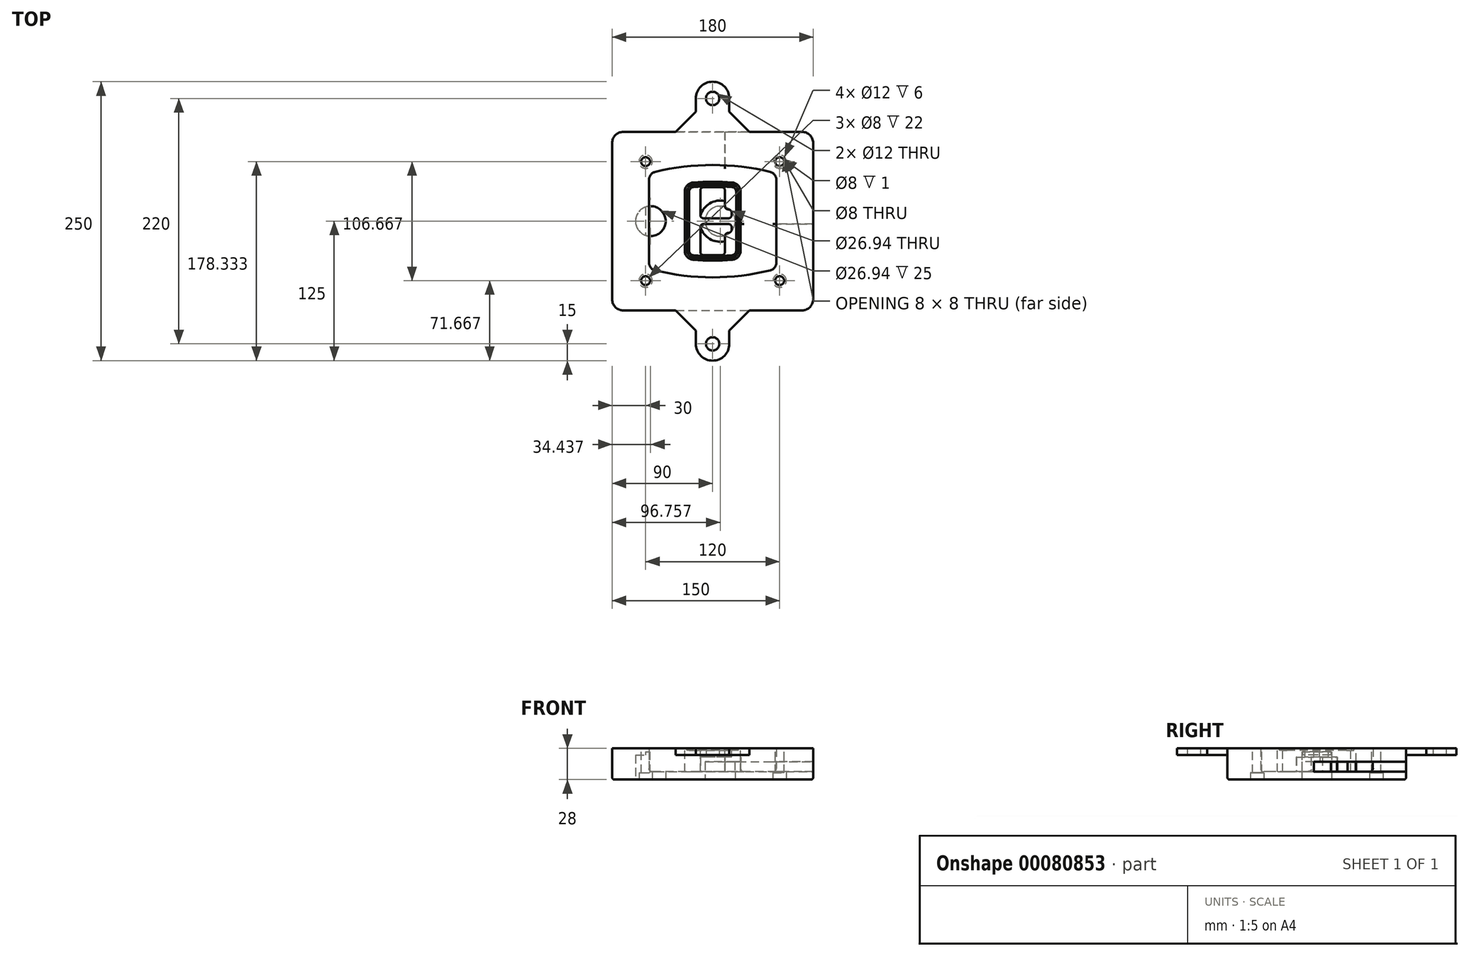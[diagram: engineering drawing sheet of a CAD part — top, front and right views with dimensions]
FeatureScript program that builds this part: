
annotation { "Feature Type Name" : "Feature", "Feature Type Description" : "" }
export const myFeature = defineFeature(function(context is Context, id is Id, definition is map)
    precondition{}
    {
        {
            var Q0;
            Q0=qCreatedBy(makeId("Top.planeOp"),FACE);
            var sketch = newSketch(context, id + "F0", { "sketchPlane" : qUnion([Q0])});
            skPoint(sketch, "E0.rect.middle", {"position": v(0, 0) * mm});
            skLineSegment(sketch, "E1.bottom", {"start": v(-80, -80) * mm, "end": v(80, -80) * mm});
            skLineSegment(sketch, "E1.top", {"start": v(-80, 80) * mm, "end": v(80, 80) * mm});
            skLineSegment(sketch, "E1.left", {"start": v(-90, -70) * mm, "end": v(-90, 70) * mm});
            skLineSegment(sketch, "E1.right", {"start": v(90, -70) * mm, "end": v(90, 70) * mm});
            skLineSegment(sketch, "E2", {"start": v(-90, 80) * mm, "end": v(90, -80) * mm, "construction": true});
            skLineSegment(sketch, "E3", {"start": v(90, 80) * mm, "end": v(-90, -80) * mm, "construction": true});
            skCircle(sketch, "E4", {"center": v(-60, 53.33) * mm, "radius": 4 * mm});
            skCircle(sketch, "E5", {"center": v(60, 53.33) * mm, "radius": 4 * mm});
            skCircle(sketch, "E6", {"center": v(60, -53.33) * mm, "radius": 4 * mm});
            skCircle(sketch, "E7", {"center": v(-60, -53.33) * mm, "radius": 4 * mm});
            skLineSegment(sketch, "E8", {"start": v(-60, 53.33) * mm, "end": v(60, 53.33) * mm, "construction": true});
            skLineSegment(sketch, "E9", {"start": v(60, 53.33) * mm, "end": v(60, -53.33) * mm, "construction": true});
            skLineSegment(sketch, "E10", {"start": v(60, -53.33) * mm, "end": v(-60, -53.33) * mm, "construction": true});
            skLineSegment(sketch, "E11", {"start": v(-60, -53.33) * mm, "end": v(-60, 53.33) * mm, "construction": true});
            skLineSegment(sketch, "E12", {"start": v(-60, 37.3) * mm, "end": v(-60, -37.3) * mm});
            skLineSegment(sketch, "E13", {"start": v(60, 37.3) * mm, "end": v(60, -37.3) * mm});
            skArc(sketch, "E14", {"start": v(52.38, 47.01) * mm, "mid": v(0, 53.33) * mm, "end": v(-52.38, 47.01) * mm});
            skArc(sketch, "E15", {"start": v(-52.38, -47.01) * mm, "mid": v(0, -53.33) * mm, "end": v(52.38, -47.01) * mm});
            skLineSegment(sketch, "E16", {"start": v(-60, 0) * mm, "end": v(60, 0) * mm, "construction": true});
            skPoint(sketch, "E17.visualSharp", {"position": v(-60, -45) * mm});
            skArc(sketch, "E17.filletArc", {"start": v(-60, -37.3) * mm, "mid": v(-57.87, -43.47) * mm, "end": v(-52.38, -47.01) * mm});
            skPoint(sketch, "E18.visualSharp", {"position": v(-60, 45) * mm});
            skArc(sketch, "E18.filletArc", {"start": v(-52.38, 47.01) * mm, "mid": v(-57.87, 43.47) * mm, "end": v(-60, 37.3) * mm});
            skPoint(sketch, "E19.visualSharp", {"position": v(60, 45) * mm});
            skArc(sketch, "E19.filletArc", {"start": v(60, 37.3) * mm, "mid": v(57.87, 43.47) * mm, "end": v(52.38, 47.01) * mm});
            skPoint(sketch, "E20.visualSharp", {"position": v(60, -45) * mm});
            skArc(sketch, "E20.filletArc", {"start": v(52.38, -47.01) * mm, "mid": v(57.87, -43.47) * mm, "end": v(60, -37.3) * mm});
            skPoint(sketch, "E21.visualSharp", {"position": v(-90, 80) * mm});
            skArc(sketch, "E21.filletArc", {"start": v(-80, 80) * mm, "mid": v(-87.07, 77.07) * mm, "end": v(-90, 70) * mm});
            skPoint(sketch, "E22.visualSharp", {"position": v(90, 80) * mm});
            skArc(sketch, "E22.filletArc", {"start": v(90, 70) * mm, "mid": v(87.07, 77.07) * mm, "end": v(80, 80) * mm});
            skPoint(sketch, "E23.visualSharp", {"position": v(90, -80) * mm});
            skArc(sketch, "E23.filletArc", {"start": v(80, -80) * mm, "mid": v(87.07, -77.07) * mm, "end": v(90, -70) * mm});
            skPoint(sketch, "E24.visualSharp", {"position": v(-90, -80) * mm});
            skArc(sketch, "E24.filletArc", {"start": v(-90, -70) * mm, "mid": v(-87.07, -77.07) * mm, "end": v(-80, -80) * mm});
            skArc(sketch, "E25.0", {"start": v(57, 37.3) * mm, "mid": v(55.5, 41.62) * mm, "end": v(51.67, 44.1) * mm});
            skLineSegment(sketch, "E25.1", {"start": v(57, 37.3) * mm, "end": v(57, -37.3) * mm});
            skArc(sketch, "E25.2", {"start": v(51.67, -44.1) * mm, "mid": v(55.5, -41.62) * mm, "end": v(57, -37.3) * mm});
            skArc(sketch, "E25.3", {"start": v(-51.67, -44.1) * mm, "mid": v(0, -50.33) * mm, "end": v(51.67, -44.1) * mm});
            skArc(sketch, "E25.4", {"start": v(-57, -37.3) * mm, "mid": v(-55.5, -41.62) * mm, "end": v(-51.67, -44.1) * mm});
            skArc(sketch, "E25.5", {"start": v(51.67, 44.1) * mm, "mid": v(0, 50.33) * mm, "end": v(-51.67, 44.1) * mm});
            skLineSegment(sketch, "E25.6", {"start": v(-57, 37.3) * mm, "end": v(-57, -37.3) * mm});
            skArc(sketch, "E25.7", {"start": v(-51.67, 44.1) * mm, "mid": v(-55.5, 41.62) * mm, "end": v(-57, 37.3) * mm});
            skArc(sketch, "E26.0", {"start": v(-53.33, 50.9) * mm, "mid": v(-61.01, 45.94) * mm, "end": v(-64, 37.3) * mm});
            skArc(sketch, "E26.1", {"start": v(53.33, 50.9) * mm, "mid": v(0, 57.33) * mm, "end": v(-53.33, 50.9) * mm});
            skArc(sketch, "E26.2", {"start": v(64, 37.3) * mm, "mid": v(61.01, 45.94) * mm, "end": v(53.33, 50.9) * mm});
            skLineSegment(sketch, "E26.3", {"start": v(64, 37.3) * mm, "end": v(64, -37.3) * mm});
            skArc(sketch, "E26.4", {"start": v(53.33, -50.9) * mm, "mid": v(61.01, -45.94) * mm, "end": v(64, -37.3) * mm});
            skLineSegment(sketch, "E26.5", {"start": v(-64, 37.3) * mm, "end": v(-64, -37.3) * mm});
            skArc(sketch, "E26.6", {"start": v(-53.33, -50.9) * mm, "mid": v(0, -57.33) * mm, "end": v(53.33, -50.9) * mm});
            skArc(sketch, "E26.7", {"start": v(-64, -37.3) * mm, "mid": v(-61.01, -45.94) * mm, "end": v(-53.33, -50.9) * mm});
            skSolve(sketch);
        }
        {
            var Q0;
            Q0=makeQuery(id+"F0.imprint","IMPRINT",FACE,{"disambiguationData":[TD([[makeQuery(id+"F0.imprint","IMPRINT",EDGE,{"derivedFrom":sQuery(id+"F0.wireOp",EDGE,"E1.bottom")}),1.0]])]});
            var Q1;
            Q1=makeQuery(id+"F0.imprint","IMPRINT",FACE,{"disambiguationData":[TD([[makeQuery(id+"F0.imprint","IMPRINT",EDGE,{"derivedFrom":sQuery(id+"F0.wireOp",EDGE,"E12")}),1.0]])]});
            var Q2;
            Q2=makeQuery(id+"F0.imprint","IMPRINT",FACE,{"disambiguationData":[TD([[makeQuery(id+"F0.imprint","IMPRINT",EDGE,{"derivedFrom":sQuery(id+"F0.wireOp",EDGE,"E25.0")}),1.0]])]});
            var Q3;
            Q3=makeQuery(id+"F0.imprint","IMPRINT",FACE,{"disambiguationData":[TD([[makeQuery(id+"F0.imprint","IMPRINT",EDGE,{"derivedFrom":sQuery(id+"F0.wireOp",EDGE,"E12")}),-1.0]])]});
            extrude(context, id + "F1", {"entities" : qUnion([Q0, Q1, Q2, Q3]), "oppositeDirection" : true, "depth" : 25 * mm});
        }
        {
            var Q0;
            Q0=makeQuery(id+"F0.imprint","IMPRINT",FACE,{"disambiguationData":[TD([[makeQuery(id+"F0.imprint","IMPRINT",EDGE,{"derivedFrom":sQuery(id+"F0.wireOp",EDGE,"E12")}),1.0]])]});
            extrude(context, id + "F2", {"entities" : qUnion([Q0]), "operationType" : NewBodyOperationType.ADD, "depth" : 3 * mm});
        }
        {
            var Q0;
            Q0=makeQuery(id+"F0.imprint","IMPRINT",FACE,{"disambiguationData":[TD([[makeQuery(id+"F0.imprint","IMPRINT",EDGE,{"derivedFrom":sQuery(id+"F0.wireOp",EDGE,"E25.0")}),1.0]])]});
            extrude(context, id + "F3", {"entities" : qUnion([Q0]), "operationType" : NewBodyOperationType.REMOVE, "oppositeDirection" : true, "depth" : 18 * mm});
        }
        {
            var Q0;
            Q0=makeQuery(id+"F2.opExtrude","CAP_FACE",FACE,{"disambiguationData":[OSD([sQuery(id+"F0.wireOp",EDGE,"E12"),sQuery(id+"F0.wireOp",EDGE,"E13"),sQuery(id+"F0.wireOp",EDGE,"E14"),sQuery(id+"F0.wireOp",EDGE,"E15"),sQuery(id+"F0.wireOp",EDGE,"E17.filletArc"),sQuery(id+"F0.wireOp",EDGE,"E18.filletArc"),sQuery(id+"F0.wireOp",EDGE,"E19.filletArc"),sQuery(id+"F0.wireOp",EDGE,"E20.filletArc"),sQuery(id+"F0.wireOp",EDGE,"E25.0"),sQuery(id+"F0.wireOp",EDGE,"E25.1"),sQuery(id+"F0.wireOp",EDGE,"E25.2"),sQuery(id+"F0.wireOp",EDGE,"E25.3"),sQuery(id+"F0.wireOp",EDGE,"E25.4"),sQuery(id+"F0.wireOp",EDGE,"E25.5"),sQuery(id+"F0.wireOp",EDGE,"E25.6"),sQuery(id+"F0.wireOp",EDGE,"E25.7")])],"isStart":false});
            var sketch = newSketch(context, id + "F4", { "sketchPlane" : qUnion([Q0])});
            skArc(sketch, "E27.0", {"start": v(-17.7, -34.56) * mm, "mid": v(0, -35.33) * mm, "end": v(17.7, -34.56) * mm});
            skArc(sketch, "E28.0", {"start": v(17.7, 34.56) * mm, "mid": v(0, 35.33) * mm, "end": v(-17.7, 34.56) * mm});
            skLineSegment(sketch, "E29", {"start": v(-25, 26.59) * mm, "end": v(-25, -26.59) * mm});
            skLineSegment(sketch, "E30", {"start": v(25, 26.59) * mm, "end": v(25, -26.59) * mm});
            skLineSegment(sketch, "E31", {"start": v(-25, 33.78) * mm, "end": v(25, 33.78) * mm, "construction": true});
            skLineSegment(sketch, "E32", {"start": v(-25, -33.78) * mm, "end": v(25, -33.78) * mm, "construction": true});
            skPoint(sketch, "E33.visualSharp", {"position": v(-25, 33.78) * mm});
            skArc(sketch, "E33.filletArc", {"start": v(-17.7, 34.56) * mm, "mid": v(-22.9, 32) * mm, "end": v(-25, 26.59) * mm});
            skPoint(sketch, "E34.visualSharp", {"position": v(25, 33.78) * mm});
            skArc(sketch, "E34.filletArc", {"start": v(25, 26.59) * mm, "mid": v(22.9, 32) * mm, "end": v(17.7, 34.56) * mm});
            skPoint(sketch, "E35.visualSharp", {"position": v(25, -33.78) * mm});
            skArc(sketch, "E35.filletArc", {"start": v(17.7, -34.56) * mm, "mid": v(22.9, -32) * mm, "end": v(25, -26.59) * mm});
            skPoint(sketch, "E36.visualSharp", {"position": v(-25, -33.78) * mm});
            skArc(sketch, "E36.filletArc", {"start": v(-25, -26.59) * mm, "mid": v(-22.9, -32) * mm, "end": v(-17.7, -34.56) * mm});
            skArc(sketch, "E37.0", {"start": v(51.67, 44.1) * mm, "mid": v(0, 50.33) * mm, "end": v(-51.67, 44.1) * mm});
            skArc(sketch, "E37.1", {"start": v(-51.67, 44.1) * mm, "mid": v(-55.5, 41.62) * mm, "end": v(-57, 37.3) * mm});
            skLineSegment(sketch, "E37.2", {"start": v(-57, 37.3) * mm, "end": v(-57, -37.3) * mm});
            skArc(sketch, "E37.3", {"start": v(-57, -37.3) * mm, "mid": v(-55.5, -41.62) * mm, "end": v(-51.67, -44.1) * mm});
            skArc(sketch, "E37.4", {"start": v(-51.67, -44.1) * mm, "mid": v(0, -50.33) * mm, "end": v(51.67, -44.1) * mm});
            skArc(sketch, "E37.5", {"start": v(51.67, -44.1) * mm, "mid": v(55.5, -41.62) * mm, "end": v(57, -37.3) * mm});
            skLineSegment(sketch, "E37.6", {"start": v(57, 37.3) * mm, "end": v(57, -37.3) * mm});
            skArc(sketch, "E37.7", {"start": v(57, 37.3) * mm, "mid": v(55.5, 41.62) * mm, "end": v(51.67, 44.1) * mm});
            skLineSegment(sketch, "E38.0", {"start": v(23, 26.59) * mm, "end": v(23, -26.59) * mm});
            skArc(sketch, "E38.1", {"start": v(17.53, -32.56) * mm, "mid": v(21.42, -30.64) * mm, "end": v(23, -26.59) * mm});
            skArc(sketch, "E38.2", {"start": v(-17.53, -32.56) * mm, "mid": v(0, -33.33) * mm, "end": v(17.53, -32.56) * mm});
            skArc(sketch, "E38.3", {"start": v(-23, -26.59) * mm, "mid": v(-21.42, -30.64) * mm, "end": v(-17.53, -32.56) * mm});
            skLineSegment(sketch, "E38.4", {"start": v(-23, 26.59) * mm, "end": v(-23, -26.59) * mm});
            skArc(sketch, "E38.5", {"start": v(23, 26.59) * mm, "mid": v(21.42, 30.64) * mm, "end": v(17.53, 32.56) * mm});
            skArc(sketch, "E38.6", {"start": v(-17.53, 32.56) * mm, "mid": v(-21.42, 30.64) * mm, "end": v(-23, 26.59) * mm});
            skArc(sketch, "E38.7", {"start": v(17.53, 32.56) * mm, "mid": v(0, 33.33) * mm, "end": v(-17.53, 32.56) * mm});
            skArc(sketch, "E39.0", {"start": v(21, 26.59) * mm, "mid": v(19.95, 29.29) * mm, "end": v(17.35, 30.57) * mm});
            skLineSegment(sketch, "E39.1", {"start": v(21, 26.59) * mm, "end": v(21, -26.59) * mm});
            skArc(sketch, "E39.2", {"start": v(17.35, -30.57) * mm, "mid": v(19.95, -29.29) * mm, "end": v(21, -26.59) * mm});
            skArc(sketch, "E39.3", {"start": v(-17.35, -30.57) * mm, "mid": v(0, -31.33) * mm, "end": v(17.35, -30.57) * mm});
            skArc(sketch, "E39.4", {"start": v(-21, -26.59) * mm, "mid": v(-19.95, -29.29) * mm, "end": v(-17.35, -30.57) * mm});
            skArc(sketch, "E39.5", {"start": v(17.35, 30.57) * mm, "mid": v(0, 31.33) * mm, "end": v(-17.35, 30.57) * mm});
            skLineSegment(sketch, "E39.6", {"start": v(-21, 26.59) * mm, "end": v(-21, -26.59) * mm});
            skArc(sketch, "E39.7", {"start": v(-17.35, 30.57) * mm, "mid": v(-19.95, 29.29) * mm, "end": v(-21, 26.59) * mm});
            skLineSegment(sketch, "E40", {"start": v(-25, 0) * mm, "end": v(25, 0) * mm, "construction": true});
            skLineSegment(sketch, "E41", {"start": v(-11, 5.5) * mm, "end": v(-11, 27.5) * mm});
            skLineSegment(sketch, "E42", {"start": v(-8, 30.5) * mm, "end": v(8, 30.5) * mm});
            skLineSegment(sketch, "E43", {"start": v(11, 27.5) * mm, "end": v(11, 13.5) * mm});
            skLineSegment(sketch, "E44", {"start": v(14, 10.5) * mm, "end": v(14, 10.5) * mm});
            skLineSegment(sketch, "E45", {"start": v(17, 7.5) * mm, "end": v(17, 5.5) * mm});
            skLineSegment(sketch, "E46", {"start": v(14, 2.5) * mm, "end": v(-8, 2.5) * mm});
            skPoint(sketch, "E47.visualSharp", {"position": v(-11, 30.5) * mm});
            skArc(sketch, "E47.filletArc", {"start": v(-8, 30.5) * mm, "mid": v(-10.12, 29.62) * mm, "end": v(-11, 27.5) * mm});
            skPoint(sketch, "E48.visualSharp", {"position": v(11, 30.5) * mm});
            skArc(sketch, "E48.filletArc", {"start": v(11, 27.5) * mm, "mid": v(10.12, 29.62) * mm, "end": v(8, 30.5) * mm});
            skPoint(sketch, "E49.visualSharp", {"position": v(11, 10.5) * mm});
            skArc(sketch, "E49.filletArc", {"start": v(11, 13.5) * mm, "mid": v(11.88, 11.38) * mm, "end": v(14, 10.5) * mm});
            skPoint(sketch, "E50.visualSharp", {"position": v(17, 10.5) * mm});
            skArc(sketch, "E50.filletArc", {"start": v(17, 7.5) * mm, "mid": v(16.12, 9.62) * mm, "end": v(14, 10.5) * mm});
            skPoint(sketch, "E51.visualSharp", {"position": v(17, 2.5) * mm});
            skArc(sketch, "E51.filletArc", {"start": v(14, 2.5) * mm, "mid": v(16.12, 3.38) * mm, "end": v(17, 5.5) * mm});
            skPoint(sketch, "E52.visualSharp", {"position": v(-11, 2.5) * mm});
            skArc(sketch, "E52.filletArc", {"start": v(-11, 5.5) * mm, "mid": v(-10.12, 3.38) * mm, "end": v(-8, 2.5) * mm});
            skLineSegment(sketch, "E53.0.MirrorCS", {"start": v(14, -2.5) * mm, "end": v(-8, -2.5) * mm});
            skArc(sketch, "E54.0.MirrorCS", {"start": v(-11, -5.5) * mm, "mid": v(-10.12, -3.38) * mm, "end": v(-8, -2.5) * mm});
            skLineSegment(sketch, "E55.0.MirrorCS", {"start": v(-11, -5.5) * mm, "end": v(-11, -27.5) * mm});
            skArc(sketch, "E56.0.MirrorCS", {"start": v(-8, -30.5) * mm, "mid": v(-10.12, -29.62) * mm, "end": v(-11, -27.5) * mm});
            skLineSegment(sketch, "E57.0.MirrorCS", {"start": v(-8, -30.5) * mm, "end": v(8, -30.5) * mm});
            skArc(sketch, "E58.0.MirrorCS", {"start": v(11, -27.5) * mm, "mid": v(10.12, -29.62) * mm, "end": v(8, -30.5) * mm});
            skLineSegment(sketch, "E59.0.MirrorCS", {"start": v(11, -27.5) * mm, "end": v(11, -13.5) * mm});
            skArc(sketch, "E60.0.MirrorCS", {"start": v(11, -13.5) * mm, "mid": v(11.88, -11.38) * mm, "end": v(14, -10.5) * mm});
            skArc(sketch, "E61.0.MirrorCS", {"start": v(17, -7.5) * mm, "mid": v(16.12, -9.62) * mm, "end": v(14, -10.5) * mm});
            skLineSegment(sketch, "E62.0.MirrorCS", {"start": v(17, -7.5) * mm, "end": v(17, -5.5) * mm});
            skArc(sketch, "E63.0.MirrorCS", {"start": v(14, -2.5) * mm, "mid": v(16.12, -3.38) * mm, "end": v(17, -5.5) * mm});
            skSolve(sketch);
        }
        {
            var Q0;
            Q0=makeQuery(id+"F4.imprint","IMPRINT",FACE,{"disambiguationData":[TD([[makeQuery(id+"F4.imprint","IMPRINT",EDGE,{"derivedFrom":sQuery(id+"F4.wireOp",EDGE,"E27.0")}),1.0]])]});
            var Q1;
            Q1=makeQuery(id+"F4.imprint","IMPRINT",FACE,{"disambiguationData":[TD([[makeQuery(id+"F4.imprint","IMPRINT",EDGE,{"derivedFrom":sQuery(id+"F4.wireOp",EDGE,"E38.0")}),-1.0]])]});
            var Q2;
            Q2=makeQuery(id+"F4.imprint","IMPRINT",FACE,{"disambiguationData":[TD([[makeQuery(id+"F4.imprint","IMPRINT",EDGE,{"derivedFrom":sQuery(id+"F4.wireOp",EDGE,"E39.0")}),1.0]])]});
            extrude(context, id + "F5", {"entities" : qUnion([Q0, Q1, Q2]), "operationType" : NewBodyOperationType.ADD, "endBound" : BoundingType.UP_TO_NEXT, "oppositeDirection" : true, "depth" : 25 * mm});
        }
        {
            var Q0;
            Q0=makeQuery(id+"F4.imprint","IMPRINT",FACE,{"disambiguationData":[TD([[makeQuery(id+"F4.imprint","IMPRINT",EDGE,{"derivedFrom":sQuery(id+"F4.wireOp",EDGE,"E38.0")}),-1.0]])]});
            extrude(context, id + "F6", {"entities" : qUnion([Q0]), "operationType" : NewBodyOperationType.REMOVE, "oppositeDirection" : true, "depth" : 2 * mm});
        }
        {
            var Q0;
            Q0=makeQuery(id+"F1.opExtrude","CAP_FACE",FACE,{"disambiguationData":[OSD([sQuery(id+"F0.wireOp",EDGE,"E1.bottom"),sQuery(id+"F0.wireOp",EDGE,"E1.top"),sQuery(id+"F0.wireOp",EDGE,"E1.left"),sQuery(id+"F0.wireOp",EDGE,"E1.right"),sQuery(id+"F0.wireOp",EDGE,"E4"),sQuery(id+"F0.wireOp",EDGE,"E5"),sQuery(id+"F0.wireOp",EDGE,"E6"),sQuery(id+"F0.wireOp",EDGE,"E7"),sQuery(id+"F0.wireOp",EDGE,"E21.filletArc"),sQuery(id+"F0.wireOp",EDGE,"E22.filletArc"),sQuery(id+"F0.wireOp",EDGE,"E23.filletArc"),sQuery(id+"F0.wireOp",EDGE,"E24.filletArc")])],"isStart":false});
            var sketch = newSketch(context, id + "F7", { "sketchPlane" : qUnion([Q0])});
            skCircle(sketch, "E64", {"center": v(6.76, 0) * mm, "radius": 13.47 * mm});
            skCircle(sketch, "E65", {"center": v(-55.56, 0) * mm, "radius": 13.47 * mm});
            skLineSegment(sketch, "E66", {"start": v(90, 0) * mm, "end": v(-90, 0) * mm});
            skCircle(sketch, "E67", {"center": v(6.76, 0) * mm, "radius": 18.47 * mm});
            skCircle(sketch, "E68", {"center": v(60, -53.33) * mm, "radius": 6 * mm});
            skCircle(sketch, "E69", {"center": v(-60, -53.33) * mm, "radius": 6 * mm});
            skCircle(sketch, "E70", {"center": v(-60, 53.33) * mm, "radius": 6 * mm});
            skCircle(sketch, "E71", {"center": v(60, 53.33) * mm, "radius": 6 * mm});
            skSolve(sketch);
        }
        {
            var Q0;
            {var subQ1=sQuery(id+"F7.wireOp",EDGE,"E66");var subQ4=sQuery(id+"F7.wireOp",EDGE,"E64");var subQ6=makeQuery(id+"F7.imprint","INTERSECT",VERTEX,{"disambiguationData":[OD(0.0)],"derivedFrom":[subQ4,subQ1]});Q0=makeQuery(id+"F7.imprint","IMPRINT",FACE,{"disambiguationData":[TD([[makeQuery(id+"F7.imprint","IMPRINT",EDGE,{"disambiguationData":[TD([[subQ6,-1.0]])],"derivedFrom":subQ4}),-1.0]])]});}
            var Q1;
            {var subQ0=sQuery(id+"F7.wireOp",EDGE,"E66");var subQ1=sQuery(id+"F7.wireOp",EDGE,"E64");var subQ3=makeQuery(id+"F7.imprint","INTERSECT",VERTEX,{"disambiguationData":[OD(0.0)],"derivedFrom":[subQ1,subQ0]});Q1=makeQuery(id+"F7.imprint","IMPRINT",FACE,{"disambiguationData":[TD([[makeQuery(id+"F7.imprint","IMPRINT",EDGE,{"disambiguationData":[TD([[subQ3,-1.0]])],"derivedFrom":subQ1}),1.0]])]});}
            var Q2;
            {var subQ0=sQuery(id+"F7.wireOp",EDGE,"E66");var subQ1=sQuery(id+"F7.wireOp",EDGE,"E64");var subQ3=makeQuery(id+"F7.imprint","INTERSECT",VERTEX,{"disambiguationData":[OD(0.0)],"derivedFrom":[subQ1,subQ0]});Q2=makeQuery(id+"F7.imprint","IMPRINT",FACE,{"disambiguationData":[TD([[makeQuery(id+"F7.imprint","IMPRINT",EDGE,{"disambiguationData":[TD([[subQ3,1.0]])],"derivedFrom":subQ1}),1.0]])]});}
            var Q3;
            {var subQ1=sQuery(id+"F7.wireOp",EDGE,"E66");var subQ4=sQuery(id+"F7.wireOp",EDGE,"E64");var subQ6=makeQuery(id+"F7.imprint","INTERSECT",VERTEX,{"disambiguationData":[OD(0.0)],"derivedFrom":[subQ4,subQ1]});Q3=makeQuery(id+"F7.imprint","IMPRINT",FACE,{"disambiguationData":[TD([[makeQuery(id+"F7.imprint","IMPRINT",EDGE,{"disambiguationData":[TD([[subQ6,1.0]])],"derivedFrom":subQ4}),-1.0]])]});}
            extrude(context, id + "F8", {"entities" : qUnion([Q0, Q1, Q2, Q3]), "operationType" : NewBodyOperationType.ADD, "oppositeDirection" : true, "depth" : 20 * mm});
        }
        {
            var Q0;
            {var subQ0=sQuery(id+"F7.wireOp",EDGE,"E66");var subQ1=sQuery(id+"F7.wireOp",EDGE,"E64");var subQ3=makeQuery(id+"F7.imprint","INTERSECT",VERTEX,{"disambiguationData":[OD(0.0)],"derivedFrom":[subQ1,subQ0]});Q0=makeQuery(id+"F7.imprint","IMPRINT",FACE,{"disambiguationData":[TD([[makeQuery(id+"F7.imprint","IMPRINT",EDGE,{"disambiguationData":[TD([[subQ3,-1.0]])],"derivedFrom":subQ1}),1.0]])]});}
            var Q1;
            {var subQ0=sQuery(id+"F7.wireOp",EDGE,"E66");var subQ1=sQuery(id+"F7.wireOp",EDGE,"E64");var subQ3=makeQuery(id+"F7.imprint","INTERSECT",VERTEX,{"disambiguationData":[OD(0.0)],"derivedFrom":[subQ1,subQ0]});Q1=makeQuery(id+"F7.imprint","IMPRINT",FACE,{"disambiguationData":[TD([[makeQuery(id+"F7.imprint","IMPRINT",EDGE,{"disambiguationData":[TD([[subQ3,1.0]])],"derivedFrom":subQ1}),1.0]])]});}
            extrude(context, id + "F9", {"entities" : qUnion([Q0, Q1]), "operationType" : NewBodyOperationType.REMOVE, "oppositeDirection" : true, "depth" : 16 * mm});
        }
        {
            var Q0;
            {var subQ0=sQuery(id+"F7.wireOp",EDGE,"E66");var subQ1=sQuery(id+"F7.wireOp",EDGE,"E65");var subQ3=makeQuery(id+"F7.imprint","INTERSECT",VERTEX,{"disambiguationData":[OD(0.0)],"derivedFrom":[subQ1,subQ0]});Q0=makeQuery(id+"F7.imprint","IMPRINT",FACE,{"disambiguationData":[TD([[makeQuery(id+"F7.imprint","IMPRINT",EDGE,{"disambiguationData":[TD([[subQ3,-1.0]])],"derivedFrom":subQ1}),1.0]])]});}
            var Q1;
            {var subQ0=sQuery(id+"F7.wireOp",EDGE,"E66");var subQ1=sQuery(id+"F7.wireOp",EDGE,"E65");var subQ3=makeQuery(id+"F7.imprint","INTERSECT",VERTEX,{"disambiguationData":[OD(0.0)],"derivedFrom":[subQ1,subQ0]});Q1=makeQuery(id+"F7.imprint","IMPRINT",FACE,{"disambiguationData":[TD([[makeQuery(id+"F7.imprint","IMPRINT",EDGE,{"disambiguationData":[TD([[subQ3,1.0]])],"derivedFrom":subQ1}),1.0]])]});}
            extrude(context, id + "F10", {"entities" : qUnion([Q0, Q1]), "operationType" : NewBodyOperationType.REMOVE, "oppositeDirection" : true, "depth" : 25 * mm});
        }
        {
            var Q0;
            Q0=makeQuery(id+"F7.imprint","IMPRINT",FACE,{"disambiguationData":[TD([[makeQuery(id+"F7.imprint","IMPRINT",EDGE,{"derivedFrom":sQuery(id+"F7.wireOp",EDGE,"E68")}),1.0]])]});
            var Q1;
            Q1=makeQuery(id+"F7.imprint","IMPRINT",FACE,{"disambiguationData":[TD([[makeQuery(id+"F7.imprint","IMPRINT",EDGE,{"derivedFrom":makeQuery(id+"F1.opExtrude","CAP_EDGE",EDGE,{"disambiguationData":[OSD([sQuery(id+"F0.wireOp",EDGE,"E5")])],"isStart":false})}),-1.0]])]});
            var Q2;
            Q2=makeQuery(id+"F7.imprint","IMPRINT",FACE,{"disambiguationData":[TD([[makeQuery(id+"F7.imprint","IMPRINT",EDGE,{"derivedFrom":sQuery(id+"F7.wireOp",EDGE,"E69")}),1.0]])]});
            var Q3;
            Q3=makeQuery(id+"F7.imprint","IMPRINT",FACE,{"disambiguationData":[TD([[makeQuery(id+"F7.imprint","IMPRINT",EDGE,{"derivedFrom":makeQuery(id+"F1.opExtrude","CAP_EDGE",EDGE,{"disambiguationData":[OSD([sQuery(id+"F0.wireOp",EDGE,"E4")])],"isStart":false})}),-1.0]])]});
            var Q4;
            Q4=makeQuery(id+"F7.imprint","IMPRINT",FACE,{"disambiguationData":[TD([[makeQuery(id+"F7.imprint","IMPRINT",EDGE,{"derivedFrom":sQuery(id+"F7.wireOp",EDGE,"E70")}),1.0]])]});
            var Q5;
            Q5=makeQuery(id+"F7.imprint","IMPRINT",FACE,{"disambiguationData":[TD([[makeQuery(id+"F7.imprint","IMPRINT",EDGE,{"derivedFrom":makeQuery(id+"F1.opExtrude","CAP_EDGE",EDGE,{"disambiguationData":[OSD([sQuery(id+"F0.wireOp",EDGE,"E7")])],"isStart":false})}),-1.0]])]});
            var Q6;
            Q6=makeQuery(id+"F7.imprint","IMPRINT",FACE,{"disambiguationData":[TD([[makeQuery(id+"F7.imprint","IMPRINT",EDGE,{"derivedFrom":sQuery(id+"F7.wireOp",EDGE,"E71")}),1.0]])]});
            var Q7;
            Q7=makeQuery(id+"F7.imprint","IMPRINT",FACE,{"disambiguationData":[TD([[makeQuery(id+"F7.imprint","IMPRINT",EDGE,{"derivedFrom":makeQuery(id+"F1.opExtrude","CAP_EDGE",EDGE,{"disambiguationData":[OSD([sQuery(id+"F0.wireOp",EDGE,"E6")])],"isStart":false})}),-1.0]])]});
            extrude(context, id + "F11", {"entities" : qUnion([Q0, Q1, Q2, Q3, Q4, Q5, Q6, Q7]), "operationType" : NewBodyOperationType.REMOVE, "oppositeDirection" : true, "depth" : 6 * mm});
        }
        {
            var Q0;
            Q0=makeQuery(id+"F9.boolean.opBoolean","COPY",FACE,{"derivedFrom":makeQuery(id+"F9.opExtrude","CAP_FACE",FACE,{"disambiguationData":[OSD([sQuery(id+"F7.wireOp",EDGE,"E64")])],"isStart":false})});
            var sketch = newSketch(context, id + "F12", { "sketchPlane" : qUnion([Q0])});
            skArc(sketch, "E72.0", {"start": v(11, -88.19) * mm, "mid": v(97.1, -83.6) * mm, "end": v(92.5, 2.5) * mm});
            skLineSegment(sketch, "E72.1", {"start": v(11, -17.97) * mm, "end": v(11, -17.97) * mm});
            skLineSegment(sketch, "E73", {"start": v(92.5, -105.13) * mm, "end": v(102.3, -105.13) * mm});
            skLineSegment(sketch, "E74.0", {"start": v(92.5, 2.5) * mm, "end": v(14, 2.5) * mm});
            skArc(sketch, "E74.1", {"start": v(14, 2.5) * mm, "mid": v(16.12, 3.38) * mm, "end": v(17, 5.5) * mm});
            skLineSegment(sketch, "E74.2", {"start": v(17, 7.5) * mm, "end": v(17, 5.5) * mm});
            skArc(sketch, "E74.3", {"start": v(17, 7.5) * mm, "mid": v(16.12, 9.62) * mm, "end": v(14, 10.5) * mm});
            skArc(sketch, "E74.4", {"start": v(11, 13.5) * mm, "mid": v(11.88, 11.38) * mm, "end": v(14, 10.5) * mm});
            skLineSegment(sketch, "E74.5", {"start": v(11, 13.5) * mm, "end": v(11, -88.19) * mm});
            skLineSegment(sketch, "E74.7", {"start": v(92.5, -2.5) * mm, "end": v(14, -2.5) * mm});
            skArc(sketch, "E74.8", {"start": v(14, -2.5) * mm, "mid": v(16.12, -3.38) * mm, "end": v(17, -5.5) * mm});
            skLineSegment(sketch, "E74.9", {"start": v(17, -7.5) * mm, "end": v(17, -5.5) * mm});
            skArc(sketch, "E74.10", {"start": v(17, -7.5) * mm, "mid": v(16.12, -9.62) * mm, "end": v(14, -10.5) * mm});
            skArc(sketch, "E74.11", {"start": v(11, -13.5) * mm, "mid": v(11.88, -11.38) * mm, "end": v(14, -10.5) * mm});
            skLineSegment(sketch, "E74.12", {"start": v(11, -17.97) * mm, "end": v(11, -13.5) * mm});
            skPoint(sketch, "E75.orphan", {"position": v(11, -27.5) * mm});
            skPoint(sketch, "E76.orphan", {"position": v(-8, -2.5) * mm});
            skPoint(sketch, "E77.orphan", {"position": v(-8, 2.5) * mm});
            skPoint(sketch, "E78.orphan", {"position": v(11, 27.5) * mm});
            skSolve(sketch);
        }
        {
            var Q0;
            {var subQ7=sQuery(id+"F12.wireOp",EDGE,"E72.0");var subQ14=sQuery(id+"F12.wireOp",EDGE,"E72.1");var subQ16=sQuery(id+"F12.wireOp",EDGE,"E74.1");var subQ18=sQuery(id+"F12.wireOp",EDGE,"E74.8");Q0=qUnion([makeQuery(id+"F12.imprint","IMPRINT",FACE,{"disambiguationData":[TD([[makeQuery(id+"F12.imprint","IMPRINT",EDGE,{"derivedFrom":subQ7}),1.0]])]}),makeQuery(id+"F12.imprint","IMPRINT",FACE,{"disambiguationData":[TD([[makeQuery(id+"F12.imprint","IMPRINT",EDGE,{"derivedFrom":subQ14}),1.0]])]}),makeQuery(id+"F12.imprint","IMPRINT",FACE,{"disambiguationData":[TD([[makeQuery(id+"F12.imprint","IMPRINT",EDGE,{"derivedFrom":subQ16}),1.0]])]}),makeQuery(id+"F12.imprint","IMPRINT",FACE,{"disambiguationData":[TD([[makeQuery(id+"F12.imprint","IMPRINT",EDGE,{"derivedFrom":subQ18}),-1.0]])]})]);}
            var Q1;
            Q1=makeQuery(id+"F5.boolean.opBoolean","SPLIT",FACE,{"disambiguationData":[TD([makeQuery(id+"F5.opExtrude","SWEPT_FACE",FACE,{"disambiguationData":[OSD([sQuery(id+"F4.wireOp",EDGE,"E41")])]})])],"derivedFrom":makeQuery(id+"F3.boolean.opBoolean","COPY",FACE,{"derivedFrom":makeQuery(id+"F3.opExtrude","CAP_FACE",FACE,{"disambiguationData":[OSD([sQuery(id+"F0.wireOp",EDGE,"E25.0"),sQuery(id+"F0.wireOp",EDGE,"E25.1"),sQuery(id+"F0.wireOp",EDGE,"E25.2"),sQuery(id+"F0.wireOp",EDGE,"E25.3"),sQuery(id+"F0.wireOp",EDGE,"E25.4"),sQuery(id+"F0.wireOp",EDGE,"E25.5"),sQuery(id+"F0.wireOp",EDGE,"E25.6"),sQuery(id+"F0.wireOp",EDGE,"E25.7")])],"isStart":false})})});
            extrude(context, id + "F13", {"entities" : qUnion([Q0]), "operationType" : NewBodyOperationType.REMOVE, "endBound" : BoundingType.UP_TO_SURFACE, "endBoundEntityFace" : qUnion([Q1]), "depth" : 25 * mm});
        }
        {
            var Q0;
            Q0=makeQuery(id+"F3.boolean.opBoolean","COPY",EDGE,{"derivedFrom":makeQuery(id+"F3.opExtrude","CAP_EDGE",EDGE,{"disambiguationData":[OSD([sQuery(id+"F0.wireOp",EDGE,"E25.6")])],"isStart":false})});
            var Q1;
            Q1=makeQuery(id+"F8.boolean.opBoolean","INTERSECT",EDGE,{"derivedFrom":[makeQuery(id+"F5.opExtrude","SWEPT_FACE",FACE,{"disambiguationData":[OSD([sQuery(id+"F4.wireOp",EDGE,"E30")])]}),makeQuery(id+"F8.opExtrude","CAP_FACE",FACE,{"disambiguationData":[OSD([sQuery(id+"F7.wireOp",EDGE,"E67")])],"isStart":false})]});
            var Q2;
            Q2=makeQuery(id+"F8.boolean.opBoolean","INTERSECT",EDGE,{"disambiguationData":[OD(1.0)],"derivedFrom":[makeQuery(id+"F5.opExtrude","SWEPT_FACE",FACE,{"disambiguationData":[OSD([sQuery(id+"F4.wireOp",EDGE,"E30")])]}),makeQuery(id+"F8.opExtrude","SWEPT_FACE",FACE,{"disambiguationData":[OSD([sQuery(id+"F7.wireOp",EDGE,"E67")])]})]});
            var Q3;
            {var subQ0=makeQuery(id+"F3.boolean.opBoolean","COPY",FACE,{"derivedFrom":makeQuery(id+"F3.opExtrude","CAP_FACE",FACE,{"disambiguationData":[OSD([sQuery(id+"F0.wireOp",EDGE,"E25.0"),sQuery(id+"F0.wireOp",EDGE,"E25.1"),sQuery(id+"F0.wireOp",EDGE,"E25.2"),sQuery(id+"F0.wireOp",EDGE,"E25.3"),sQuery(id+"F0.wireOp",EDGE,"E25.4"),sQuery(id+"F0.wireOp",EDGE,"E25.5"),sQuery(id+"F0.wireOp",EDGE,"E25.6"),sQuery(id+"F0.wireOp",EDGE,"E25.7")])],"isStart":false})});var subQ1=sQuery(id+"F4.wireOp",EDGE,"E30");Q3=makeQuery(id+"F8.boolean.opBoolean","SPLIT",EDGE,{"disambiguationData":[TD([makeQuery(id+"F5.opExtrude","SWEPT_FACE",FACE,{"disambiguationData":[OSD([sQuery(id+"F4.wireOp",EDGE,"E35.filletArc")])]})])],"derivedFrom":makeQuery(id+"F5.opExtrude","TWEAK_EDGE",EDGE,{"derivedFrom":[subQ0,makeQuery(id+"F4.imprint","IMPRINT",EDGE,{"derivedFrom":subQ1})]})});}
            var Q4;
            {var subQ0=sQuery(id+"F0.wireOp",EDGE,"E25.0");var subQ1=sQuery(id+"F0.wireOp",EDGE,"E25.1");var subQ2=sQuery(id+"F0.wireOp",EDGE,"E25.2");var subQ3=sQuery(id+"F0.wireOp",EDGE,"E25.3");var subQ4=sQuery(id+"F0.wireOp",EDGE,"E25.4");var subQ5=sQuery(id+"F0.wireOp",EDGE,"E25.5");var subQ6=sQuery(id+"F0.wireOp",EDGE,"E25.6");var subQ7=sQuery(id+"F0.wireOp",EDGE,"E25.7");Q4=makeQuery(id+"F8.boolean.opBoolean","INTERSECT",EDGE,{"derivedFrom":[makeQuery(id+"F5.boolean.opBoolean","SPLIT",FACE,{"disambiguationData":[TD([makeQuery(id+"F2.opExtrude","SWEPT_FACE",FACE,{"disambiguationData":[OSD([subQ0])]})])],"derivedFrom":makeQuery(id+"F3.boolean.opBoolean","COPY",FACE,{"derivedFrom":makeQuery(id+"F3.opExtrude","CAP_FACE",FACE,{"disambiguationData":[OSD([subQ0,subQ1,subQ2,subQ3,subQ4,subQ5,subQ6,subQ7])],"isStart":false})})}),makeQuery(id+"F8.opExtrude","SWEPT_FACE",FACE,{"disambiguationData":[OSD([sQuery(id+"F7.wireOp",EDGE,"E67")])]})]});}
            var Q5;
            Q5=makeQuery(id+"F8.boolean.opBoolean","INTERSECT",EDGE,{"disambiguationData":[OD(0.0)],"derivedFrom":[makeQuery(id+"F5.opExtrude","SWEPT_FACE",FACE,{"disambiguationData":[OSD([sQuery(id+"F4.wireOp",EDGE,"E30")])]}),makeQuery(id+"F8.opExtrude","SWEPT_FACE",FACE,{"disambiguationData":[OSD([sQuery(id+"F7.wireOp",EDGE,"E67")])]})]});
            fillet(context, id + "F14", {"entities" : qUnion([Q0, Q1, Q2, Q3, Q4, Q5]), "radius" : 3 * mm, "tangentPropagation" : true, "allowEdgeOverflow" : false});
        }
        {
            var Q0;
            Q0=makeQuery(id+"F1.opExtrude","CAP_EDGE",EDGE,{"disambiguationData":[OSD([sQuery(id+"F0.wireOp",EDGE,"E1.bottom")])],"isStart":false});
            fillet(context, id + "F15", {"entities" : qUnion([Q0]), "radius" : 2 * mm, "tangentPropagation" : true, "allowEdgeOverflow" : false});
        }
        {
            var Q0;
            {var subQ0=sQuery(id+"F0.wireOp",EDGE,"E22.filletArc");var subQ1=sQuery(id+"F0.wireOp",EDGE,"E7");var subQ2=sQuery(id+"F0.wireOp",EDGE,"E6");var subQ3=sQuery(id+"F0.wireOp",EDGE,"E5");var subQ4=sQuery(id+"F0.wireOp",EDGE,"E4");var subQ5=sQuery(id+"F0.wireOp",EDGE,"E1.bottom");var subQ6=sQuery(id+"F0.wireOp",EDGE,"E21.filletArc");var subQ7=sQuery(id+"F0.wireOp",EDGE,"E1.top");var subQ8=sQuery(id+"F0.wireOp",EDGE,"E1.left");var subQ9=sQuery(id+"F0.wireOp",EDGE,"E1.right");var subQ10=sQuery(id+"F0.wireOp",EDGE,"E23.filletArc");var subQ11=sQuery(id+"F0.wireOp",EDGE,"E24.filletArc");Q0=makeQuery(id+"F2.boolean.opBoolean","SPLIT",FACE,{"disambiguationData":[TD([makeQuery(id+"F1.opExtrude","SWEPT_FACE",FACE,{"disambiguationData":[OSD([subQ5])]})])],"derivedFrom":makeQuery(id+"F1.opExtrude","CAP_FACE",FACE,{"disambiguationData":[OSD([subQ5,subQ7,subQ8,subQ9,subQ4,subQ3,subQ2,subQ1,subQ6,subQ0,subQ10,subQ11])],"isStart":true})});}
            var sketch = newSketch(context, id + "F16", { "sketchPlane" : qUnion([Q0])});
            skLineSegment(sketch, "E79.0", {"start": v(-80, 80) * mm, "end": v(80, 80) * mm});
            skArc(sketch, "E79.1", {"start": v(-80, 80) * mm, "mid": v(-87.07, 77.07) * mm, "end": v(-90, 70) * mm});
            skLineSegment(sketch, "E79.2", {"start": v(-90, -70) * mm, "end": v(-90, 70) * mm});
            skArc(sketch, "E79.3", {"start": v(-90, -70) * mm, "mid": v(-87.07, -77.07) * mm, "end": v(-80, -80) * mm});
            skLineSegment(sketch, "E79.4", {"start": v(-80, -80) * mm, "end": v(80, -80) * mm});
            skArc(sketch, "E79.5", {"start": v(80, -80) * mm, "mid": v(87.07, -77.07) * mm, "end": v(90, -70) * mm});
            skLineSegment(sketch, "E79.6", {"start": v(90, -70) * mm, "end": v(90, 70) * mm});
            skArc(sketch, "E79.7", {"start": v(90, 70) * mm, "mid": v(87.07, 77.07) * mm, "end": v(80, 80) * mm});
            skCircle(sketch, "E79.8", {"center": v(-60, 53.33) * mm, "radius": 4 * mm});
            skCircle(sketch, "E79.9", {"center": v(-60, -53.33) * mm, "radius": 4 * mm});
            skCircle(sketch, "E79.10", {"center": v(60, -53.33) * mm, "radius": 4 * mm});
            skCircle(sketch, "E79.11", {"center": v(60, 53.33) * mm, "radius": 4 * mm});
            skArc(sketch, "E79.12", {"start": v(52.38, 47.01) * mm, "mid": v(0, 53.33) * mm, "end": v(-52.38, 47.01) * mm});
            skArc(sketch, "E79.13", {"start": v(-52.38, 47.01) * mm, "mid": v(-57.87, 43.47) * mm, "end": v(-60, 37.3) * mm});
            skLineSegment(sketch, "E79.14", {"start": v(-60, 37.3) * mm, "end": v(-60, -37.3) * mm});
            skArc(sketch, "E79.15", {"start": v(-60, -37.3) * mm, "mid": v(-57.87, -43.47) * mm, "end": v(-52.38, -47.01) * mm});
            skArc(sketch, "E79.16", {"start": v(-52.38, -47.01) * mm, "mid": v(0, -53.33) * mm, "end": v(52.38, -47.01) * mm});
            skArc(sketch, "E79.17", {"start": v(52.38, -47.01) * mm, "mid": v(57.87, -43.47) * mm, "end": v(60, -37.3) * mm});
            skLineSegment(sketch, "E79.18", {"start": v(60, 37.3) * mm, "end": v(60, -37.3) * mm});
            skArc(sketch, "E79.19", {"start": v(60, 37.3) * mm, "mid": v(57.87, 43.47) * mm, "end": v(52.38, 47.01) * mm});
            skLineSegment(sketch, "E80", {"start": v(0, 80) * mm, "end": v(0, 110) * mm, "construction": true});
            skPoint(sketch, "E80.endSnap0", {"position": v(0, 80) * mm});
            skCircle(sketch, "E81", {"center": v(0, 110) * mm, "radius": 6 * mm});
            skLineSegment(sketch, "E82", {"start": v(-33.07, 80) * mm, "end": v(-15.07, 98) * mm});
            skLineSegment(sketch, "E83", {"start": v(-15.07, 98) * mm, "end": v(-15.07, 110) * mm});
            skLineSegment(sketch, "E84", {"start": v(32.93, 80) * mm, "end": v(14.93, 98) * mm});
            skLineSegment(sketch, "E85", {"start": v(14.93, 98) * mm, "end": v(14.93, 110) * mm});
            skArc(sketch, "E86", {"start": v(14.93, 110) * mm, "mid": v(-0.07, 125) * mm, "end": v(-15.07, 110) * mm});
            skLineSegment(sketch, "E87", {"start": v(-90, 0) * mm, "end": v(90, 0) * mm, "construction": true});
            skLineSegment(sketch, "E88.MirrorCS", {"start": v(-33.07, -80) * mm, "end": v(-15.07, -98) * mm});
            skLineSegment(sketch, "E89.MirrorCS", {"start": v(-15.07, -98) * mm, "end": v(-15.07, -110) * mm});
            skArc(sketch, "E90.MirrorCS", {"start": v(14.93, -110) * mm, "mid": v(-0.07, -125) * mm, "end": v(-15.07, -110) * mm});
            skLineSegment(sketch, "E91.MirrorCS", {"start": v(14.93, -98) * mm, "end": v(14.93, -110) * mm});
            skLineSegment(sketch, "E92.MirrorCS", {"start": v(32.93, -80) * mm, "end": v(14.93, -98) * mm});
            skCircle(sketch, "E93.MirrorC", {"center": v(0, -110) * mm, "radius": 6 * mm});
            skSolve(sketch);
        }
        {
            var Q0;
            Q0 = qSketchRegion(id + "F16", true);
            extrude(context, id + "F17", {"entities" : qUnion([Q0]), "operationType" : NewBodyOperationType.ADD, "endBound" : BoundingType.SYMMETRIC, "depth" : 6 * mm});
        }
    });
